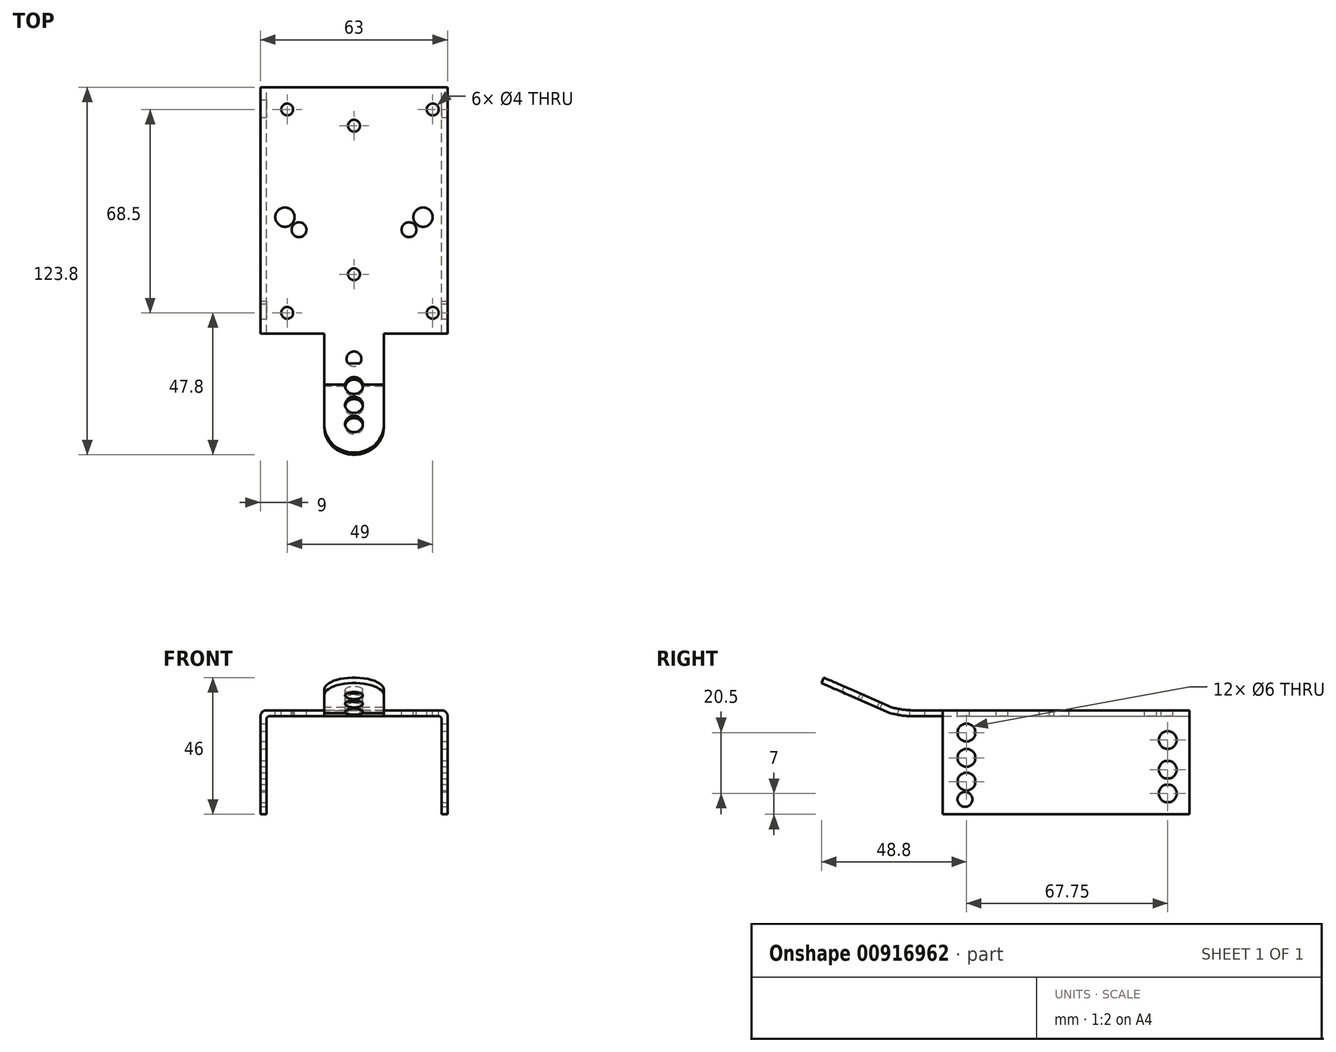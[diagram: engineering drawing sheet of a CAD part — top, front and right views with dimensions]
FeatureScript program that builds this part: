
annotation { "Feature Type Name" : "Feature", "Feature Type Description" : "" }
export const myFeature = defineFeature(function(context is Context, id is Id, definition is map)
    precondition{}
    {
        {
            var Q0;
            Q0=qCreatedBy(makeId("Front.planeOp"),FACE);
            var sketch = newSketch(context, id + "F0", { "sketchPlane" : qUnion([Q0])});
            skLineSegment(sketch, "E0.bottom", {"start": v(0, 0) * mm, "end": v(2, 0) * mm});
            skLineSegment(sketch, "E0.top", {"start": v(2, 35) * mm, "end": v(61, 35) * mm});
            skLineSegment(sketch, "E0.left", {"start": v(0, 0) * mm, "end": v(0, 33) * mm});
            skLineSegment(sketch, "E0.right", {"start": v(63, 0) * mm, "end": v(63, 33) * mm});
            skLineSegment(sketch, "E1.0", {"start": v(3, 33) * mm, "end": v(60, 33) * mm});
            skLineSegment(sketch, "E2.0", {"start": v(61, 0) * mm, "end": v(61, 32) * mm});
            skLineSegment(sketch, "E3.3", {"start": v(2, 33) * mm, "end": v(61, 33) * mm});
            skLineSegment(sketch, "E4.0", {"start": v(2, 0) * mm, "end": v(2, 32) * mm});
            skLineSegment(sketch, "E5.trimOffspring", {"start": v(61, 0) * mm, "end": v(63, 0) * mm});
            skPoint(sketch, "E6.visualSharp", {"position": v(2, 33) * mm});
            skArc(sketch, "E6.filletArc", {"start": v(3, 33) * mm, "mid": v(2.3, 32.7) * mm, "end": v(2, 32) * mm});
            skPoint(sketch, "E7.visualSharp", {"position": v(0, 35) * mm});
            skArc(sketch, "E7.filletArc", {"start": v(2, 35) * mm, "mid": v(0.59, 34.41) * mm, "end": v(0, 33) * mm});
            skPoint(sketch, "E8.visualSharp", {"position": v(63, 35) * mm});
            skArc(sketch, "E8.filletArc", {"start": v(63, 33) * mm, "mid": v(62.41, 34.41) * mm, "end": v(61, 35) * mm});
            skArc(sketch, "E9.filletArc", {"start": v(61, 32) * mm, "mid": v(60.7, 32.7) * mm, "end": v(60, 33) * mm});
            skSolve(sketch);
        }
        {
            var Q0;
            Q0=makeQuery(id+"F0.imprint","IMPRINT",FACE,{"disambiguationData":[TD([[makeQuery(id+"F0.imprint","IMPRINT",EDGE,{"derivedFrom":sQuery(id+"F0.wireOp",EDGE,"E0.bottom")}),1.0]])]});
            extrude(context, id + "F1", {"entities" : qUnion([Q0]), "depth" : 83 * mm, "offsetDistance" : 25 * mm});
        }
        {
            var Q0;
            Q0=makeQuery(id+"F1.opExtrude","SWEPT_FACE",FACE,{"disambiguationData":[OSD([sQuery(id+"F0.wireOp",EDGE,"E0.right")])]});
            var sketch = newSketch(context, id + "F2", { "sketchPlane" : qUnion([Q0])});
            skCircle(sketch, "E10", {"center": v(-7.25, 7) * mm, "radius": 3 * mm});
            skCircle(sketch, "E11", {"center": v(-7.25, 15) * mm, "radius": 3 * mm});
            skCircle(sketch, "E12", {"center": v(-7.25, 25) * mm, "radius": 3 * mm});
            skCircle(sketch, "E13", {"center": v(-75.5, 5) * mm, "radius": 2.5 * mm});
            skCircle(sketch, "E14", {"center": v(-75, 11) * mm, "radius": 3 * mm});
            skCircle(sketch, "E15", {"center": v(-75, 19) * mm, "radius": 3 * mm});
            skCircle(sketch, "E16", {"center": v(-75, 27.5) * mm, "radius": 3 * mm});
            skSolve(sketch);
        }
        {
            var Q0;
            Q0 = qSketchRegion(id + "F2", true);
            extrude(context, id + "F3", {"entities" : qUnion([Q0]), "operationType" : NewBodyOperationType.REMOVE, "endBound" : BoundingType.THROUGH_ALL, "oppositeDirection" : true, "depth" : 25 * mm, "offsetDistance" : 25 * mm});
        }
        {
            var Q0;
            Q0=makeQuery(id+"F1.opExtrude","SWEPT_FACE",FACE,{"disambiguationData":[OSD([sQuery(id+"F0.wireOp",EDGE,"E0.right")])]});
            var Q1;
            Q1=makeQuery(id+"F1.opExtrude","SWEPT_FACE",FACE,{"disambiguationData":[OSD([sQuery(id+"F0.wireOp",EDGE,"E0.left")])]});
            cPlane(context, id + "F4", {"entities" : qUnion([Q0, Q1]), "cplaneType" : CPlaneType.MID_PLANE, "offset" : 25 * mm, "width" : 150 * mm, "height" : 150 * mm});
        }
        {
            var Q0;
            Q0=qCreatedBy(id+"F4.planeOp",FACE);
            var sketch = newSketch(context, id + "F5", { "sketchPlane" : qUnion([Q0])});
            skLineSegment(sketch, "E17", {"start": v(-83, 35) * mm, "end": v(-93, 35) * mm});
            skLineSegment(sketch, "E18", {"start": v(-100.09, 36) * mm, "end": v(-123, 46) * mm});
            skLineSegment(sketch, "E19.0", {"start": v(-100.77, 34.12) * mm, "end": v(-123.8, 44.17) * mm});
            skLineSegment(sketch, "E20.0", {"start": v(-83, 33) * mm, "end": v(-93, 33) * mm});
            skLineSegment(sketch, "E21", {"start": v(-123, 46) * mm, "end": v(-123.8, 44.17) * mm});
            skArc(sketch, "E22", {"start": v(-93, 33) * mm, "mid": v(-96.92, 33.28) * mm, "end": v(-100.77, 34.12) * mm});
            skArc(sketch, "E23.0", {"start": v(-93, 35) * mm, "mid": v(-96.58, 35.25) * mm, "end": v(-100.09, 36) * mm});
            skLineSegment(sketch, "E24", {"start": v(-83, 35) * mm, "end": v(-83, 33) * mm});
            skSolve(sketch);
        }
        {
            var Q0;
            Q0 = qSketchRegion(id + "F5", true);
            extrude(context, id + "F6", {"entities" : qUnion([Q0]), "operationType" : NewBodyOperationType.ADD, "depth" : 10 * mm, "offsetDistance" : 25 * mm, "hasSecondDirection" : true, "secondDirectionOppositeDirection" : true, "secondDirectionDepth" : 10 * mm});
        }
        {
            var Q0;
            Q0=makeQuery(id+"F6.opExtrude","CAP_EDGE",EDGE,{"disambiguationData":[OSD([sQuery(id+"F5.wireOp",EDGE,"E21")])],"isStart":false});
            var Q1;
            Q1=makeQuery(id+"F6.opExtrude","CAP_EDGE",EDGE,{"disambiguationData":[OSD([sQuery(id+"F5.wireOp",EDGE,"E21")])],"isStart":true});
            fillet(context, id + "F7", {"entities" : qUnion([Q0, Q1]), "radius" : 10 * mm, "tangentPropagation" : true, "allowEdgeOverflow" : false});
        }
        {
            var Q0;
            Q0=makeQuery(id+"F6.boolean.opBoolean","MERGE",FACE,{"derivedFrom":[makeQuery(id+"F1.opExtrude","SWEPT_FACE",FACE,{"disambiguationData":[OSD([sQuery(id+"F0.wireOp",EDGE,"E0.top")])]}),makeQuery(id+"F6.opExtrude","SWEPT_FACE",FACE,{"disambiguationData":[OSD([sQuery(id+"F5.wireOp",EDGE,"E17")])]})]});
            var sketch = newSketch(context, id + "F8", { "sketchPlane" : qUnion([Q0])});
            skCircle(sketch, "E25", {"center": v(31.5, -91.5) * mm, "radius": 2.5 * mm});
            skPoint(sketch, "E25.centerSnap0", {"position": v(31.5, -93) * mm});
            skSolve(sketch);
        }
        {
            var Q0;
            Q0 = qSketchRegion(id + "F8", true);
            extrude(context, id + "F9", {"entities" : qUnion([Q0]), "operationType" : NewBodyOperationType.REMOVE, "endBound" : BoundingType.THROUGH_ALL, "oppositeDirection" : true, "depth" : 25 * mm, "offsetDistance" : 25 * mm});
        }
        {
            var Q0;
            Q0=makeQuery(id+"F6.opExtrude","SWEPT_FACE",FACE,{"disambiguationData":[OSD([sQuery(id+"F5.wireOp",EDGE,"E18")])]});
            var sketch = newSketch(context, id + "F10", { "sketchPlane" : qUnion([Q0])});
            skCircle(sketch, "E26", {"center": v(31.5, -120.63) * mm, "radius": 3 * mm});
            skPoint(sketch, "E26.centerSnap0", {"position": v(31.5, -131.13) * mm});
            skCircle(sketch, "E27", {"center": v(31.5, -113.63) * mm, "radius": 3 * mm});
            skCircle(sketch, "E28", {"center": v(31.5, -106.63) * mm, "radius": 3 * mm});
            skSolve(sketch);
        }
        {
            var Q0;
            Q0=makeQuery(id+"F10.imprint","IMPRINT",FACE,{"disambiguationData":[TD([[makeQuery(id+"F10.imprint","IMPRINT",EDGE,{"derivedFrom":sQuery(id+"F10.wireOp",EDGE,"E27")}),1.0]])]});
            var Q1;
            Q1=makeQuery(id+"F10.imprint","IMPRINT",FACE,{"disambiguationData":[TD([[makeQuery(id+"F10.imprint","IMPRINT",EDGE,{"derivedFrom":sQuery(id+"F10.wireOp",EDGE,"E26")}),1.0]])]});
            var Q2;
            {var subQ0=sQuery(id+"F10.wireOp",EDGE,"E28");var subQ1=makeQuery(id+"F6.opExtrude","SWEPT_EDGE",EDGE,{"disambiguationData":[OSD([sQuery(id+"F5.wireOp",EDGE,"E18"),sQuery(id+"F5.wireOp",EDGE,"E23.0")])]});var subQ2=makeQuery(id+"F10.imprint","INTERSECT",VERTEX,{"disambiguationData":[OD(0.0)],"derivedFrom":[subQ1,subQ0]});Q2=makeQuery(id+"F10.imprint","IMPRINT",FACE,{"disambiguationData":[TD([[makeQuery(id+"F10.imprint","IMPRINT",EDGE,{"disambiguationData":[TD([[subQ2,1.0]])],"derivedFrom":subQ0}),1.0]])]});}
            var Q3;
            {var subQ0=sQuery(id+"F10.wireOp",EDGE,"E28");var subQ1=makeQuery(id+"F6.opExtrude","SWEPT_EDGE",EDGE,{"disambiguationData":[OSD([sQuery(id+"F5.wireOp",EDGE,"E18"),sQuery(id+"F5.wireOp",EDGE,"E23.0")])]});var subQ2=makeQuery(id+"F10.imprint","INTERSECT",VERTEX,{"disambiguationData":[OD(0.0)],"derivedFrom":[subQ1,subQ0]});Q3=makeQuery(id+"F10.imprint","IMPRINT",FACE,{"disambiguationData":[TD([[makeQuery(id+"F10.imprint","IMPRINT",EDGE,{"disambiguationData":[TD([[subQ2,-1.0]])],"derivedFrom":subQ0}),1.0]])]});}
            extrude(context, id + "F11", {"entities" : qUnion([Q0, Q1, Q2, Q3]), "operationType" : NewBodyOperationType.REMOVE, "oppositeDirection" : true, "depth" : 25 * mm, "offsetDistance" : 25 * mm, "hasSecondDirection" : true, "secondDirectionOppositeDirection" : false, "secondDirectionDepth" : 25 * mm});
        }
        {
            var Q0;
            Q0=makeQuery(id+"F6.boolean.opBoolean","MERGE",FACE,{"derivedFrom":[makeQuery(id+"F1.opExtrude","SWEPT_FACE",FACE,{"disambiguationData":[OSD([sQuery(id+"F0.wireOp",EDGE,"E0.top")])]}),makeQuery(id+"F6.opExtrude","SWEPT_FACE",FACE,{"disambiguationData":[OSD([sQuery(id+"F5.wireOp",EDGE,"E17")])]})]});
            var sketch = newSketch(context, id + "F12", { "sketchPlane" : qUnion([Q0])});
            skCircle(sketch, "E29", {"center": v(9, -7.5) * mm, "radius": 2 * mm});
            skCircle(sketch, "E30", {"center": v(58, -7.5) * mm, "radius": 2 * mm});
            skCircle(sketch, "E31", {"center": v(9, -76) * mm, "radius": 2 * mm});
            skCircle(sketch, "E32", {"center": v(58, -76) * mm, "radius": 2 * mm});
            skCircle(sketch, "E33", {"center": v(31.5, -13) * mm, "radius": 2 * mm});
            skCircle(sketch, "E34", {"center": v(31.5, -63) * mm, "radius": 2 * mm});
            skCircle(sketch, "E35", {"center": v(50, -48) * mm, "radius": 2.5 * mm});
            skCircle(sketch, "E36", {"center": v(13, -48) * mm, "radius": 2.5 * mm});
            skCircle(sketch, "E37", {"center": v(8.25, -43.75) * mm, "radius": 3.25 * mm});
            skCircle(sketch, "E38", {"center": v(54.75, -43.75) * mm, "radius": 3.25 * mm});
            skSolve(sketch);
        }
        {
            var Q0;
            Q0 = qSketchRegion(id + "F12", true);
            extrude(context, id + "F13", {"entities" : qUnion([Q0]), "operationType" : NewBodyOperationType.REMOVE, "endBound" : BoundingType.THROUGH_ALL, "oppositeDirection" : true, "depth" : 25 * mm, "offsetDistance" : 25 * mm});
        }
    });
